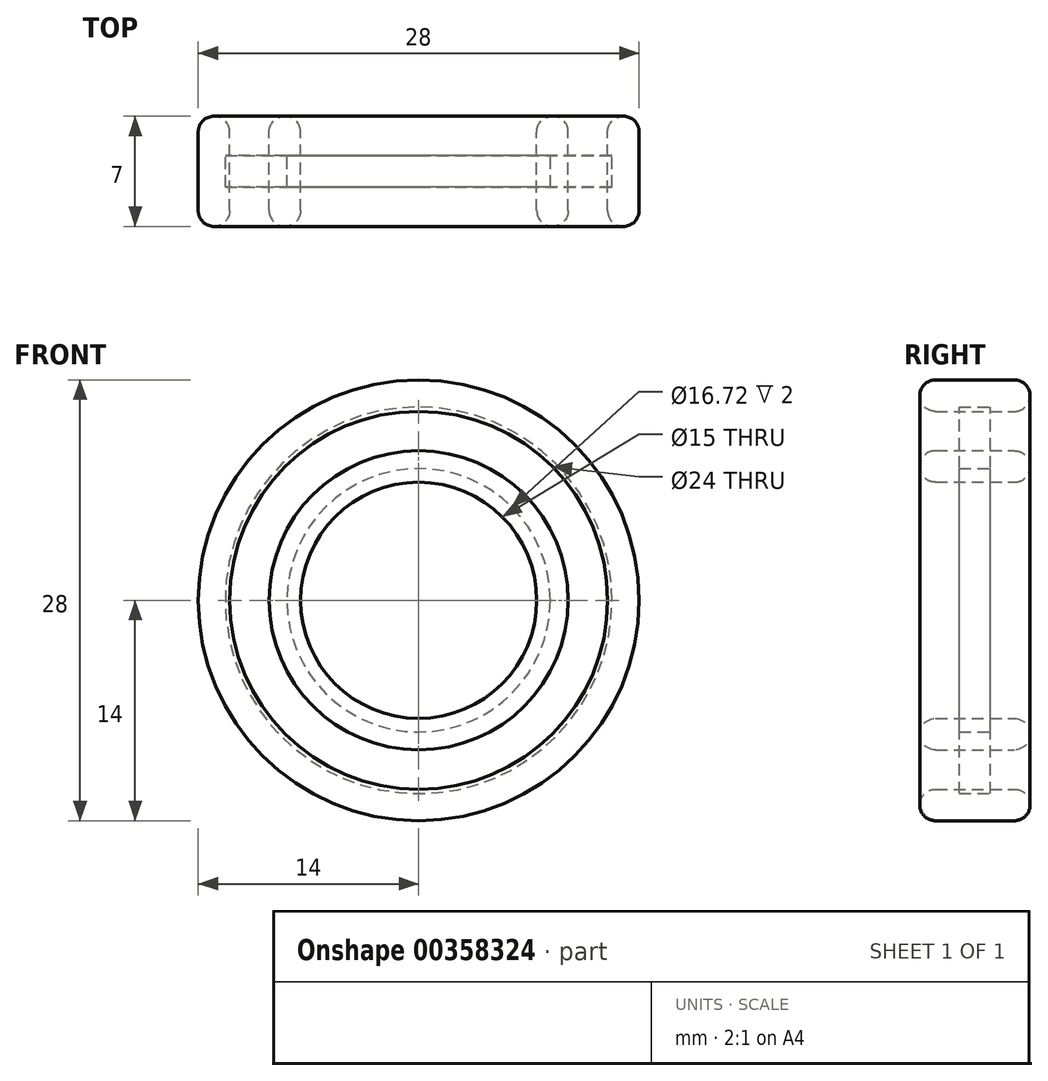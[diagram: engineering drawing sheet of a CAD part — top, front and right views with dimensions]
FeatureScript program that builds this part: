
annotation { "Feature Type Name" : "Feature", "Feature Type Description" : "" }
export const myFeature = defineFeature(function(context is Context, id is Id, definition is map)
    precondition{}
    {
        {
            var Q0;
            Q0=qCreatedBy(makeId("Front.planeOp"),FACE);
            var sketch = newSketch(context, id + "F0", { "sketchPlane" : qUnion([Q0])});
            skCircle(sketch, "E0", {"center": v(0, 0) * mm, "radius": 14 * mm});
            skCircle(sketch, "E1.0", {"center": v(0, 0) * mm, "radius": 12 * mm});
            skSolve(sketch);
        }
        {
            var Q0;
            Q0=makeQuery(id+"F0.imprint","IMPRINT",FACE,{"disambiguationData":[TD([[makeQuery(id+"F0.imprint","IMPRINT",EDGE,{"derivedFrom":sQuery(id+"F0.wireOp",EDGE,"E0")}),1.0]])]});
            extrude(context, id + "F1", {"entities" : qUnion([Q0]), "depth" : 3.5 * mm, "hasSecondDirection" : true, "secondDirectionOppositeDirection" : true, "secondDirectionDepth" : 3.5 * mm});
        }
        {
            var Q0;
            Q0=qCreatedBy(makeId("Front.planeOp"),FACE);
            var sketch = newSketch(context, id + "F2", { "sketchPlane" : qUnion([Q0])});
            skCircle(sketch, "E2", {"center": v(0, 0) * mm, "radius": 7.5 * mm});
            skCircle(sketch, "E3.0", {"center": v(0, 0) * mm, "radius": 9.5 * mm});
            skSolve(sketch);
        }
        {
            var Q0;
            Q0=makeQuery(id+"F2.imprint","IMPRINT",FACE,{"disambiguationData":[TD([[makeQuery(id+"F2.imprint","IMPRINT",EDGE,{"derivedFrom":sQuery(id+"F2.wireOp",EDGE,"E2")}),-1.0]])]});
            extrude(context, id + "F3", {"entities" : qUnion([Q0]), "depth" : 3.5 * mm, "hasSecondDirection" : true, "secondDirectionOppositeDirection" : true, "secondDirectionDepth" : 3.5 * mm});
        }
        {
            var Q0;
            Q0=qCreatedBy(makeId("Front.planeOp"),FACE);
            var sketch = newSketch(context, id + "F4", { "sketchPlane" : qUnion([Q0])});
            skCircle(sketch, "E4", {"center": v(0, 0) * mm, "radius": 12.28 * mm});
            skCircle(sketch, "E5", {"center": v(0, 0) * mm, "radius": 8.36 * mm});
            skSolve(sketch);
        }
        {
            var Q0;
            Q0=makeQuery(id+"F4.imprint","IMPRINT",FACE,{"disambiguationData":[TD([[makeQuery(id+"F4.imprint","IMPRINT",EDGE,{"derivedFrom":sQuery(id+"F4.wireOp",EDGE,"E4")}),1.0]])]});
            extrude(context, id + "F5", {"entities" : qUnion([Q0]), "depth" : 1 * mm, "hasSecondDirection" : true, "secondDirectionOppositeDirection" : true, "secondDirectionDepth" : 1 * mm});
        }
        {
            var Q0;
            Q0=makeQuery(id+"F1.opExtrude","CAP_EDGE",EDGE,{"disambiguationData":[OSD([sQuery(id+"F0.wireOp",EDGE,"E1.0")])],"isStart":false});
            var Q1;
            Q1=makeQuery(id+"F1.opExtrude","CAP_EDGE",EDGE,{"disambiguationData":[OSD([sQuery(id+"F0.wireOp",EDGE,"E0")])],"isStart":false});
            var Q2;
            Q2=makeQuery(id+"F3.opExtrude","CAP_EDGE",EDGE,{"disambiguationData":[OSD([sQuery(id+"F2.wireOp",EDGE,"E3.0")])],"isStart":false});
            var Q3;
            Q3=makeQuery(id+"F3.opExtrude","CAP_EDGE",EDGE,{"disambiguationData":[OSD([sQuery(id+"F2.wireOp",EDGE,"E2")])],"isStart":false});
            var Q4;
            Q4=makeQuery(id+"F3.opExtrude","CAP_EDGE",EDGE,{"disambiguationData":[OSD([sQuery(id+"F2.wireOp",EDGE,"E2")])],"isStart":true});
            var Q5;
            Q5=makeQuery(id+"F3.opExtrude","CAP_EDGE",EDGE,{"disambiguationData":[OSD([sQuery(id+"F2.wireOp",EDGE,"E3.0")])],"isStart":true});
            var Q6;
            Q6=makeQuery(id+"F1.opExtrude","CAP_EDGE",EDGE,{"disambiguationData":[OSD([sQuery(id+"F0.wireOp",EDGE,"E1.0")])],"isStart":true});
            var Q7;
            Q7=makeQuery(id+"F1.opExtrude","CAP_EDGE",EDGE,{"disambiguationData":[OSD([sQuery(id+"F0.wireOp",EDGE,"E0")])],"isStart":true});
            fillet(context, id + "F6", {"entities" : qUnion([Q0, Q1, Q2, Q3, Q4, Q5, Q6, Q7]), "radius" : 1 * mm, "tangentPropagation" : true, "allowEdgeOverflow" : false});
        }
    });
